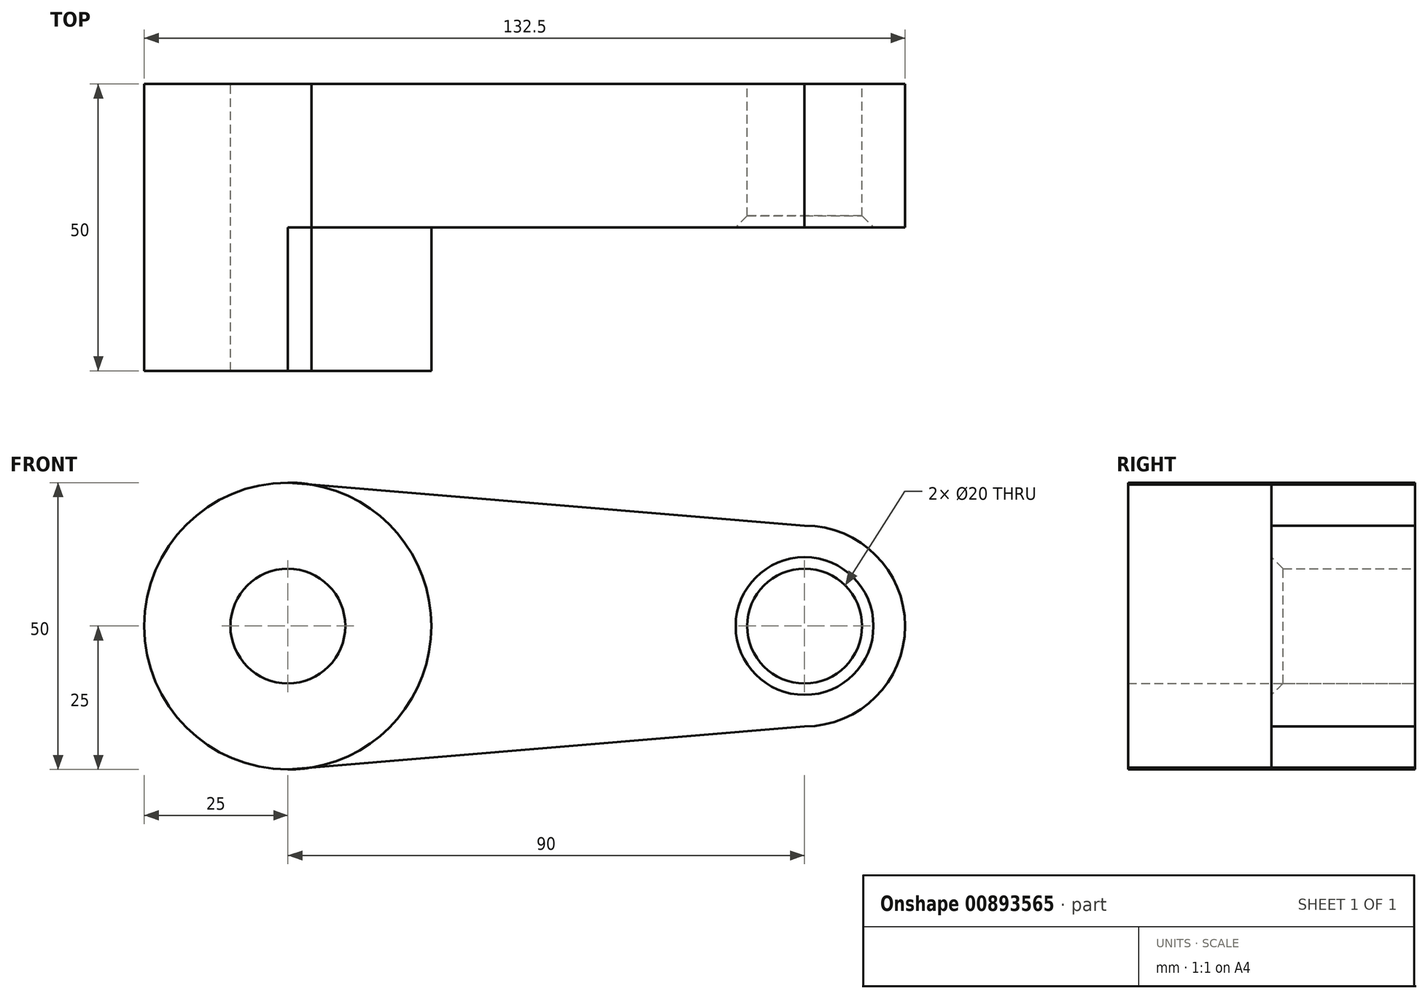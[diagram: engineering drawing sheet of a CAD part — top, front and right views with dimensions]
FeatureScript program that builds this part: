
annotation { "Feature Type Name" : "Feature", "Feature Type Description" : "" }
export const myFeature = defineFeature(function(context is Context, id is Id, definition is map)
    precondition{}
    {
        {
            var Q0;
            Q0=qCreatedBy(makeId("Front.planeOp"),FACE);
            var sketch = newSketch(context, id + "F0", { "sketchPlane" : qUnion([Q0])});
            skCircle(sketch, "E0", {"center": v(0, 0) * mm, "radius": 25 * mm});
            skCircle(sketch, "E1", {"center": v(90, 0) * mm, "radius": 17.5 * mm});
            skLineSegment(sketch, "E2", {"start": v(0, 25) * mm, "end": v(90, 17.5) * mm});
            skLineSegment(sketch, "E3", {"start": v(0, -25) * mm, "end": v(90, -17.5) * mm});
            skCircle(sketch, "E4", {"center": v(0, 0) * mm, "radius": 10 * mm});
            skCircle(sketch, "E5", {"center": v(90, 0) * mm, "radius": 10 * mm});
            skSolve(sketch);
        }
        {
            var Q0;
            Q0 = qSketchRegion(id + "F0", true);
            extrude(context, id + "F1", {"entities" : qUnion([Q0]), "depth" : 25 * mm, "offsetDistance" : 25 * mm});
        }
        {
            var Q0;
            Q0=makeQuery(id+"F0.imprint","IMPRINT",FACE,{"disambiguationData":[TD([[makeQuery(id+"F0.imprint","IMPRINT",EDGE,{"derivedFrom":sQuery(id+"F0.wireOp",EDGE,"E4")}),-1.0]])]});
            extrude(context, id + "F2", {"entities" : qUnion([Q0]), "operationType" : NewBodyOperationType.ADD, "depth" : 50 * mm, "offsetDistance" : 25 * mm});
        }
        {
            var Q0;
            {var subQ0=sQuery(id+"F0.wireOp",EDGE,"E0");Q0=makeQuery(id+"F2.opExtrude","CAP_EDGE",EDGE,{"disambiguationData":[OSD([subQ0]),TDD([makeQuery(id+"F0.imprint","IMPRINT",EDGE,{"disambiguationData":[TD([[makeQuery(id+"F0.imprint","INTERSECT",VERTEX,{"disambiguationData":[OD(1.0)],"derivedFrom":[subQ0,sQuery(id+"F0.wireOp",EDGE,"E2")]}),1.0]])],"derivedFrom":subQ0})])],"isStart":false});}
            var Q1;
            {var subQ0=sQuery(id+"F0.wireOp",EDGE,"E0");Q1=makeQuery(id+"F2.opExtrude","CAP_EDGE",EDGE,{"disambiguationData":[OSD([subQ0]),TDD([makeQuery(id+"F0.imprint","IMPRINT",EDGE,{"disambiguationData":[TD([[makeQuery(id+"F0.imprint","INTERSECT",VERTEX,{"disambiguationData":[OD(0.0)],"derivedFrom":[subQ0,sQuery(id+"F0.wireOp",EDGE,"E2")]}),-1.0]])],"derivedFrom":subQ0})])],"isStart":false});}
            var Q2;
            Q2=makeQuery(id+"F1.opExtrude","CAP_EDGE",EDGE,{"disambiguationData":[OSD([sQuery(id+"F0.wireOp",EDGE,"E5")])],"isStart":false});
            chamfer(context, id + "F3", {"entities" : qUnion([Q0, Q1, Q2]), "width" : 2 * mm, "tangentPropagation" : true});
        }
    });
